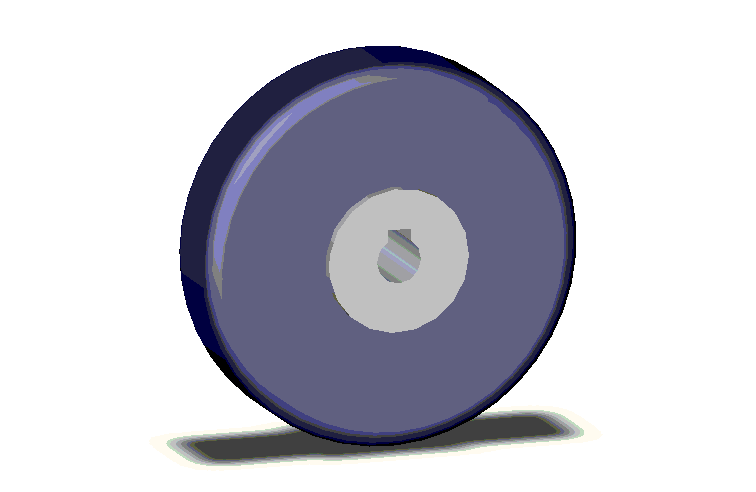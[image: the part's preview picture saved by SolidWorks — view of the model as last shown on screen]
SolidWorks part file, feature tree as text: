
SOLIDWORKS PART (.sldprt)
format: sldprt  version: not decoded by parser v0  size: 142,848 bytes
history: native  units: mm
features: sketch x4, extrude x2, cut_extrude x2, plane x1, fillet x1 (+8 scaffold rows collapsed)
feature tree (18):
  scaffold x8  (default folders/planes/origin — collapsed)
  sketch  "Sketch1"  dims[D1=19.05mm]
  extrude  "Base-Extrude"  Depth=15.875mm
  plane  "Plane1"  Offset=1.27mm
  sketch  "Sketch2"  dims[D1=50.8mm]
  extrude  "Boss-Extrude1"  Depth=13.335mm
  fillet  "Fillet1"  Radius=2.54mm
  sketch  "Sketch3"  dims[D1=6.0mm]
  cut_extrude  "Cut-Extrude1"  [1 undecoded]
  sketch  "Sketch4"  dims[D1=1.5875mm D2=3.175mm D3=1.5875mm]
  cut_extrude  "Cut-Extrude2"  [1 undecoded]
decode coverage: 7 of 9 modeling features carry decoded parameters
note: 2 parameter values undecoded
note: suppression state not decoded; provenance and decode notes live in map.json
